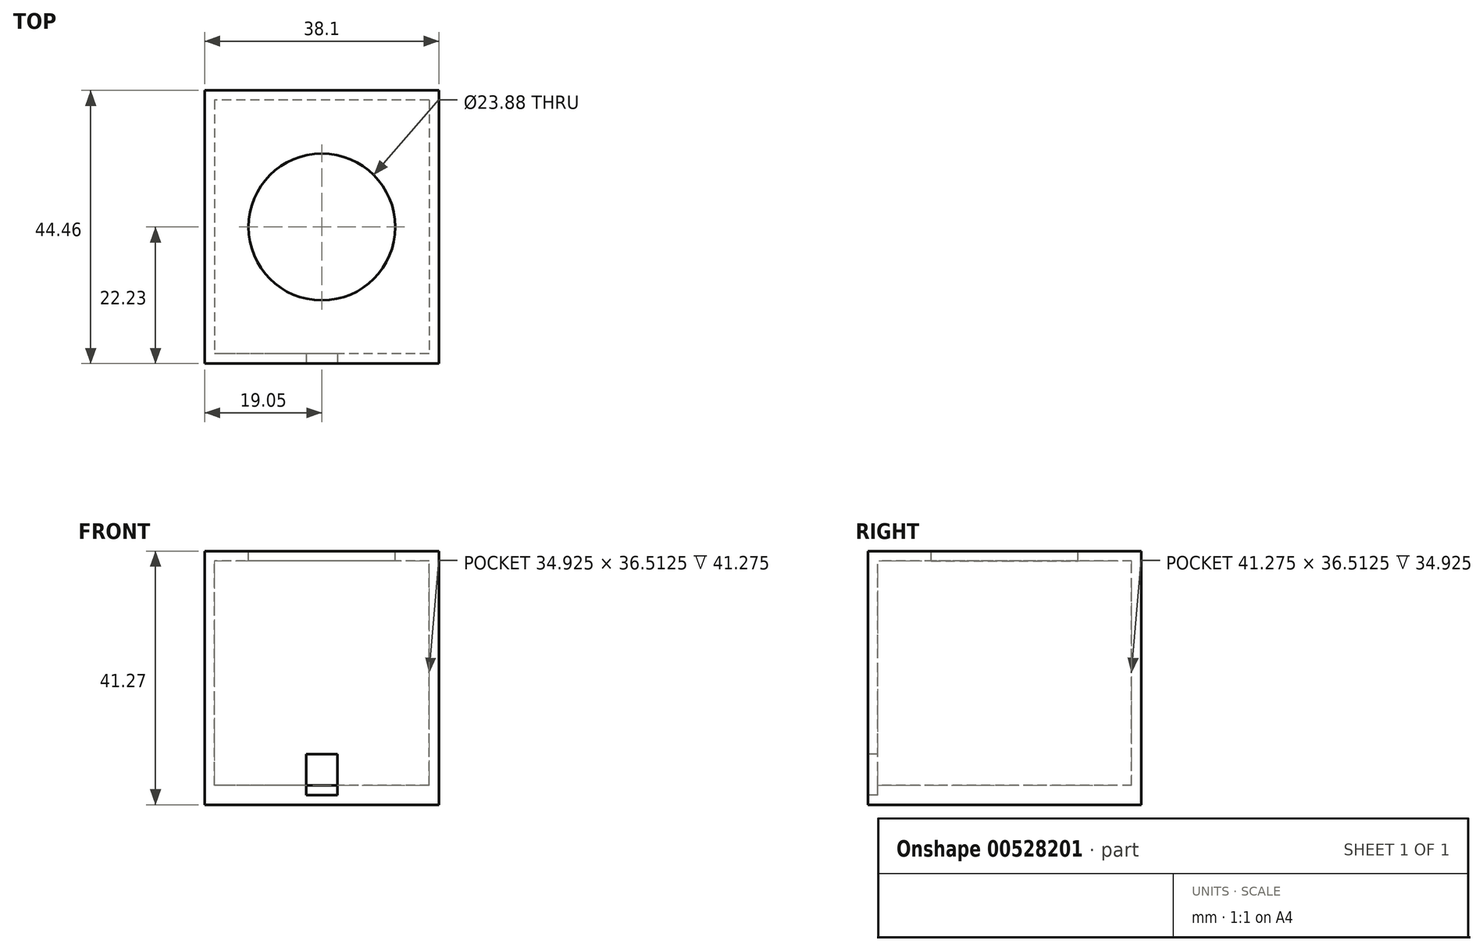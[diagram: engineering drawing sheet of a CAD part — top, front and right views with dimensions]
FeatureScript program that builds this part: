
annotation { "Feature Type Name" : "Feature", "Feature Type Description" : "" }
export const myFeature = defineFeature(function(context is Context, id is Id, definition is map)
    precondition{}
    {
        {
            var Q0;
            Q0=qCreatedBy(makeId("Top.planeOp"),FACE);
            var sketch = newSketch(context, id + "F0", { "sketchPlane" : qUnion([Q0])});
            skCircle(sketch, "E0", {"center": v(0, 0) * mm, "radius": 11.94 * mm});
            skLineSegment(sketch, "E1.bottom", {"start": v(19.05, 22.23) * mm, "end": v(-19.05, 22.23) * mm});
            skLineSegment(sketch, "E1.top", {"start": v(19.05, -22.23) * mm, "end": v(-19.05, -22.23) * mm});
            skLineSegment(sketch, "E1.left", {"start": v(19.05, 22.23) * mm, "end": v(19.05, -22.23) * mm});
            skLineSegment(sketch, "E1.right", {"start": v(-19.05, 22.23) * mm, "end": v(-19.05, -22.23) * mm});
            skSolve(sketch);
        }
        {
            var Q0;
            Q0 = qSketchRegion(id + "F0", true);
            extrude(context, id + "F1", {"entities" : qUnion([Q0]), "oppositeDirection" : true, "depth" : 1.59 * mm, "offsetDistance" : 25.4 * mm});
        }
        {
            var Q0;
            Q0=makeQuery(id+"F1.opExtrude","CAP_FACE",FACE,{"disambiguationData":[OSD([sQuery(id+"F0.wireOp",EDGE,"E0"),sQuery(id+"F0.wireOp",EDGE,"E1.bottom"),sQuery(id+"F0.wireOp",EDGE,"E1.top"),sQuery(id+"F0.wireOp",EDGE,"E1.left"),sQuery(id+"F0.wireOp",EDGE,"E1.right")])],"isStart":false});
            var sketch = newSketch(context, id + "F2", { "sketchPlane" : qUnion([Q0])});
            skLineSegment(sketch, "E2.0", {"start": v(17.46, 20.64) * mm, "end": v(-17.46, 20.64) * mm});
            skLineSegment(sketch, "E2.1", {"start": v(17.46, -20.64) * mm, "end": v(17.46, 20.64) * mm});
            skLineSegment(sketch, "E2.2", {"start": v(17.46, -20.64) * mm, "end": v(-17.46, -20.64) * mm});
            skLineSegment(sketch, "E2.3", {"start": v(-17.46, -20.64) * mm, "end": v(-17.46, 20.64) * mm});
            skLineSegment(sketch, "E3.0", {"start": v(19.05, 22.23) * mm, "end": v(-19.05, 22.23) * mm});
            skLineSegment(sketch, "E4.0", {"start": v(-19.05, -22.23) * mm, "end": v(-19.05, 22.23) * mm});
            skLineSegment(sketch, "E5.0", {"start": v(19.05, -22.23) * mm, "end": v(19.05, 22.23) * mm});
            skLineSegment(sketch, "E6.0", {"start": v(19.05, -22.23) * mm, "end": v(-19.05, -22.23) * mm});
            skSolve(sketch);
        }
        {
            var Q0;
            Q0 = qSketchRegion(id + "F2", true);
            extrude(context, id + "F3", {"entities" : qUnion([Q0]), "operationType" : NewBodyOperationType.ADD, "depth" : 38.1 * mm, "offsetDistance" : 25.4 * mm});
        }
        {
            var Q0;
            Q0=makeQuery(id+"F3.boolean.opBoolean","MERGE",FACE,{"derivedFrom":[makeQuery(id+"F1.opExtrude","SWEPT_FACE",FACE,{"disambiguationData":[OSD([sQuery(id+"F0.wireOp",EDGE,"E1.top")])]}),makeQuery(id+"F3.opExtrude","SWEPT_FACE",FACE,{"disambiguationData":[OSD([sQuery(id+"F2.wireOp",EDGE,"E3.0")])]})]});
            var sketch = newSketch(context, id + "F4", { "sketchPlane" : qUnion([Q0])});
            skLineSegment(sketch, "E7.bottom", {"start": v(2.54, -39.69) * mm, "end": v(-2.54, -39.69) * mm});
            skLineSegment(sketch, "E7.top", {"start": v(2.54, -33.02) * mm, "end": v(-2.54, -33.02) * mm});
            skLineSegment(sketch, "E7.left", {"start": v(2.54, -39.69) * mm, "end": v(2.54, -33.02) * mm});
            skLineSegment(sketch, "E7.right", {"start": v(-2.54, -39.69) * mm, "end": v(-2.54, -33.02) * mm});
            skPoint(sketch, "E7.middle", {"position": v(0, -36.35) * mm});
            skLineSegment(sketch, "E8", {"start": v(0, 0) * mm, "end": v(0, -39.69) * mm, "construction": true});
            skSolve(sketch);
        }
        {
            var Q0;
            Q0 = qSketchRegion(id + "F4", true);
            extrude(context, id + "F5", {"entities" : qUnion([Q0]), "operationType" : NewBodyOperationType.REMOVE, "endBound" : BoundingType.UP_TO_NEXT, "oppositeDirection" : true, "depth" : 25.4 * mm, "offsetDistance" : 25.4 * mm});
        }
        {
            var Q0;
            Q0=makeQuery(id+"F3.opExtrude","CAP_FACE",FACE,{"disambiguationData":[OSD([sQuery(id+"F2.wireOp",EDGE,"E2.0"),sQuery(id+"F2.wireOp",EDGE,"E2.1"),sQuery(id+"F2.wireOp",EDGE,"E2.2"),sQuery(id+"F2.wireOp",EDGE,"E2.3"),sQuery(id+"F2.wireOp",EDGE,"E3.0"),sQuery(id+"F2.wireOp",EDGE,"E4.0"),sQuery(id+"F2.wireOp",EDGE,"E5.0"),sQuery(id+"F2.wireOp",EDGE,"E6.0")])],"isStart":false});
            var sketch = newSketch(context, id + "F6", { "sketchPlane" : qUnion([Q0])});
            skLineSegment(sketch, "E9.0", {"start": v(2.54, 22.23) * mm, "end": v(-2.54, 22.23) * mm});
            skLineSegment(sketch, "E9.1", {"start": v(2.54, 22.23) * mm, "end": v(-2.54, 22.23) * mm});
            skPoint(sketch, "E9.4", {"position": v(0, 22.23) * mm});
            skLineSegment(sketch, "E9.10", {"start": v(19.05, 22.23) * mm, "end": v(-19.05, 22.23) * mm});
            skLineSegment(sketch, "E9.11", {"start": v(-19.05, -22.23) * mm, "end": v(-19.05, 22.23) * mm});
            skLineSegment(sketch, "E9.12", {"start": v(19.05, -22.23) * mm, "end": v(19.05, 22.23) * mm});
            skLineSegment(sketch, "E9.13", {"start": v(19.05, -22.23) * mm, "end": v(-19.05, -22.23) * mm});
            skSolve(sketch);
        }
        {
            var Q0;
            Q0 = qSketchRegion(id + "F6", true);
            extrude(context, id + "F7", {"entities" : qUnion([Q0]), "depth" : 1.59 * mm, "offsetDistance" : 25.4 * mm});
        }
        {
            var Q0;
            Q0=makeQuery(id+"F7.opExtrude","CAP_FACE",FACE,{"disambiguationData":[OSD([sQuery(id+"F6.wireOp",EDGE,"E9.10"),sQuery(id+"F6.wireOp",EDGE,"E9.11"),sQuery(id+"F6.wireOp",EDGE,"E9.12"),sQuery(id+"F6.wireOp",EDGE,"E9.13")])],"isStart":true});
            var sketch = newSketch(context, id + "F8", { "sketchPlane" : qUnion([Q0])});
            skLineSegment(sketch, "E10.0", {"start": v(-17.46, 20.64) * mm, "end": v(-17.46, -20.64) * mm});
            skLineSegment(sketch, "E11.0", {"start": v(17.46, 20.64) * mm, "end": v(-17.46, 20.64) * mm});
            skLineSegment(sketch, "E12.0", {"start": v(17.46, 20.64) * mm, "end": v(17.46, -20.64) * mm});
            skLineSegment(sketch, "E13.0", {"start": v(17.46, -20.64) * mm, "end": v(-17.46, -20.64) * mm});
            skSolve(sketch);
        }
        {
            var Q0;
            Q0 = qSketchRegion(id + "F8", true);
            extrude(context, id + "F9", {"entities" : qUnion([Q0]), "operationType" : NewBodyOperationType.ADD, "depth" : 1.59 * mm, "offsetDistance" : 25.4 * mm});
        }
    });
